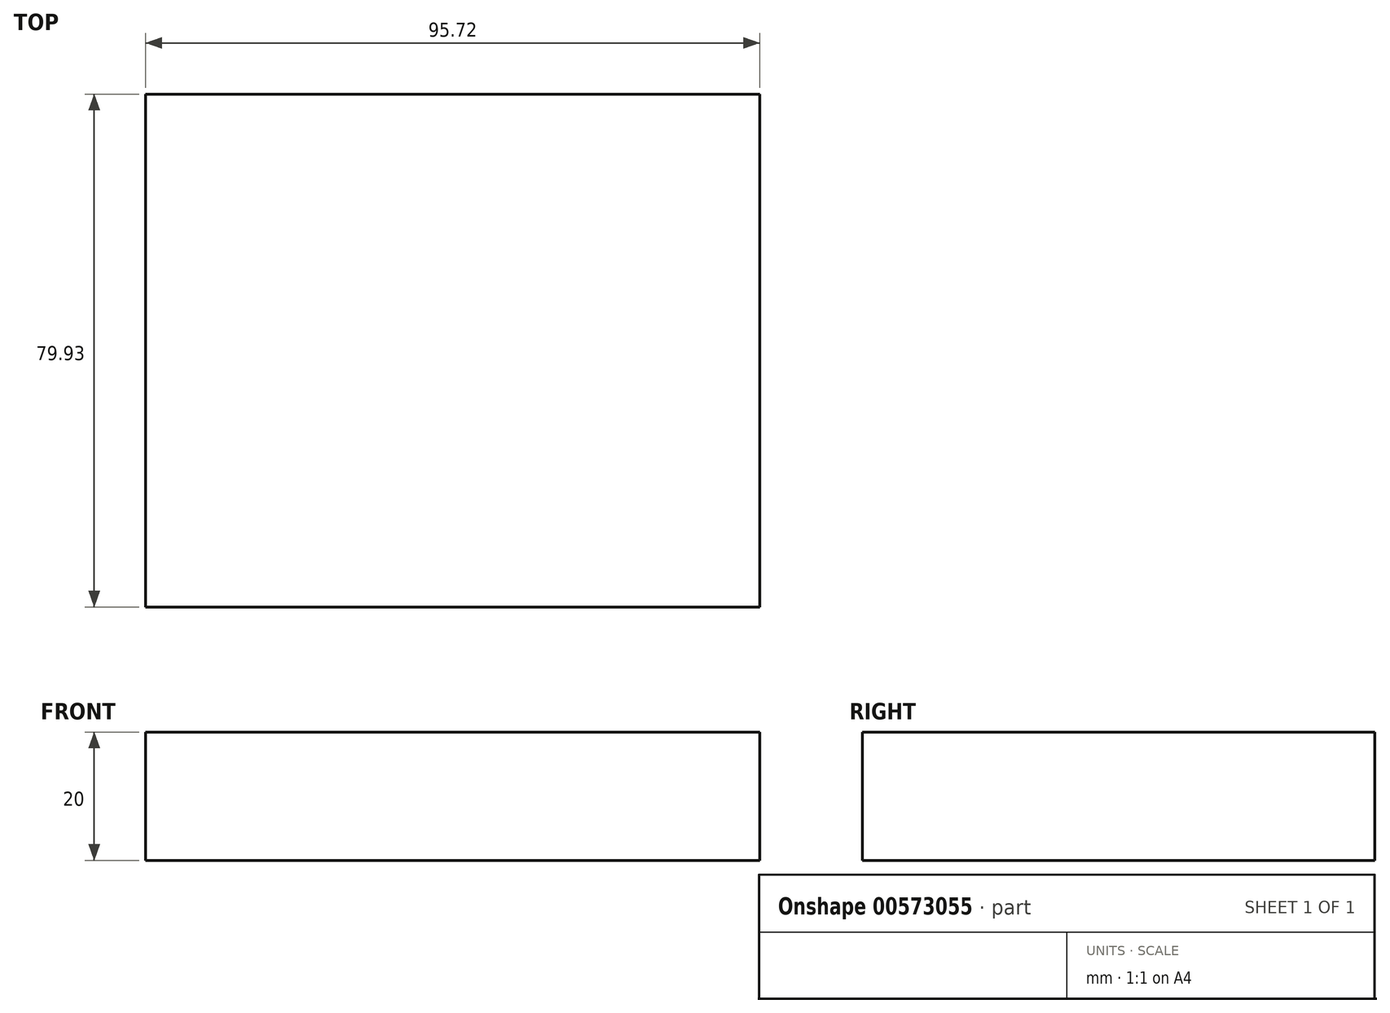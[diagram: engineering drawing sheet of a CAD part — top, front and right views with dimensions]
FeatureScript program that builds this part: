
annotation { "Feature Type Name" : "Feature", "Feature Type Description" : "" }
export const myFeature = defineFeature(function(context is Context, id is Id, definition is map)
    precondition{}
    {
        {
            var Q0;
            Q0=qCreatedBy(makeId("Top.planeOp"),FACE);
            var sketch = newSketch(context, id + "F0", { "sketchPlane" : qUnion([Q0])});
            skLineSegment(sketch, "E0", {"start": v(-53.52, 42.91) * mm, "end": v(-53.52, -37.02) * mm});
            skLineSegment(sketch, "E1", {"start": v(-53.52, 42.91) * mm, "end": v(42.2, 42.91) * mm});
            skLineSegment(sketch, "E2", {"start": v(42.2, 42.91) * mm, "end": v(42.2, -37.02) * mm});
            skLineSegment(sketch, "E3", {"start": v(-53.52, -37.02) * mm, "end": v(42.2, -37.02) * mm});
            skSolve(sketch);
        }
        {
            var Q0;
            Q0=makeQuery(id+"F0.imprint","IMPRINT",FACE,{"disambiguationData":[TD([[makeQuery(id+"F0.imprint","IMPRINT",EDGE,{"derivedFrom":sQuery(id+"F0.wireOp",EDGE,"E0")}),1.0]])]});
            extrude(context, id + "F1", {"entities" : qUnion([Q0]), "depth" : 20 * mm, "offsetDistance" : 25 * mm});
        }
    });
